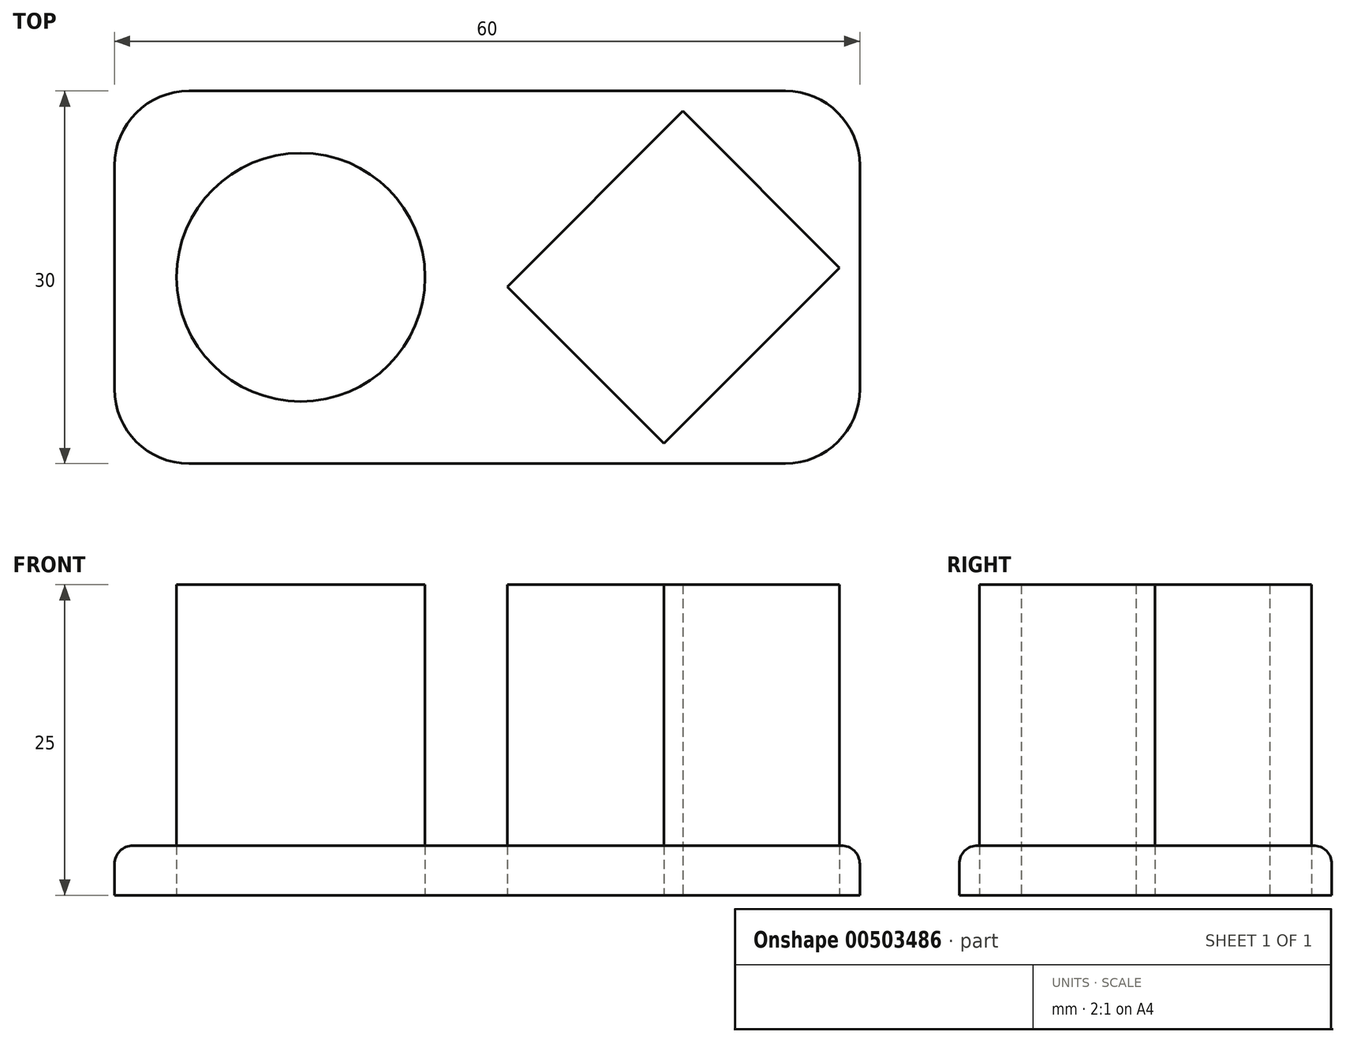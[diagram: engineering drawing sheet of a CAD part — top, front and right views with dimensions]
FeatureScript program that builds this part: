
annotation { "Feature Type Name" : "Feature", "Feature Type Description" : "" }
export const myFeature = defineFeature(function(context is Context, id is Id, definition is map)
    precondition{}
    {
        {
            var Q0;
            Q0=qCreatedBy(makeId("Top.planeOp"),FACE);
            var sketch = newSketch(context, id + "F0", { "sketchPlane" : qUnion([Q0])});
            skLineSegment(sketch, "E0.bottom", {"start": v(30, -15) * mm, "end": v(-30, -15) * mm});
            skLineSegment(sketch, "E0.top", {"start": v(30, 15) * mm, "end": v(-30, 15) * mm});
            skLineSegment(sketch, "E0.left", {"start": v(30, -15) * mm, "end": v(30, 15) * mm});
            skLineSegment(sketch, "E0.right", {"start": v(-30, -15) * mm, "end": v(-30, 15) * mm});
            skPoint(sketch, "E0.middle", {"position": v(0, 0) * mm});
            skSolve(sketch);
        }
        {
            var Q0;
            Q0 = qSketchRegion(id + "F0", true);
            extrude(context, id + "F1", {"entities" : qUnion([Q0]), "depth" : 4 * mm});
        }
        {
            var Q0;
            Q0=qCreatedBy(makeId("Top.planeOp"),FACE);
            var sketch = newSketch(context, id + "F2", { "sketchPlane" : qUnion([Q0])});
            skLineSegment(sketch, "E1", {"start": v(0, 0) * mm, "end": v(15, 0) * mm});
            skLineSegment(sketch, "E2", {"start": v(0, 0) * mm, "end": v(-15, 0) * mm});
            skCircle(sketch, "E3", {"center": v(-15, 0) * mm, "radius": 10 * mm});
            skLineSegment(sketch, "E4.bottom", {"start": v(25, -8.92) * mm, "end": v(5, -8.92) * mm});
            skLineSegment(sketch, "E4.top", {"start": v(25, 8.92) * mm, "end": v(5, 8.92) * mm});
            skLineSegment(sketch, "E4.left", {"start": v(25, -8.92) * mm, "end": v(25, 8.92) * mm});
            skLineSegment(sketch, "E4.right", {"start": v(5, -8.92) * mm, "end": v(5, 8.92) * mm});
            skPoint(sketch, "E4.middle", {"position": v(15, 0) * mm});
            skSolve(sketch);
        }
        {
            var Q0;
            Q0 = qSketchRegion(id + "F2", true);
            extrude(context, id + "F3", {"entities" : qUnion([Q0]), "depth" : 25 * mm});
        }
        {
            var Q0;
            Q0=qCreatedBy(makeId("Front.planeOp"),FACE);
            var sketch = newSketch(context, id + "F4", { "sketchPlane" : qUnion([Q0])});
            skLineSegment(sketch, "E5", {"start": v(0, 0) * mm, "end": v(15, 0) * mm});
            skLineSegment(sketch, "E6", {"start": v(15, 0) * mm, "end": v(15, 40) * mm});
            skSolve(sketch);
        }
        {
            var Q0;
            Q0=makeQuery(id+"F3.opExtrude","SWEPT_BODY",BODY,{"disambiguationData":[OSD([sQuery(id+"F2.wireOp",EDGE,"E4.bottom"),sQuery(id+"F2.wireOp",EDGE,"E4.top"),sQuery(id+"F2.wireOp",EDGE,"E4.left"),sQuery(id+"F2.wireOp",EDGE,"E4.right")])]});
            var Q1;
            Q1=sQuery(id+"F4.wireOp",EDGE,"E6");
            transform(context, id + "F5", {"entities" : qUnion([Q0]), "transformType" : TransformType.ROTATION, "transformAxis" : qUnion([Q1]), "angle" : 45 * degree, "makeCopy" : false});
        }
        {
            var Q0;
            Q0=makeQuery(id+"F1.opExtrude","SWEPT_EDGE",EDGE,{"disambiguationData":[OSD([sQuery(id+"F0.wireOp",EDGE,"E0.bottom"),sQuery(id+"F0.wireOp",EDGE,"E0.right")])]});
            var Q1;
            Q1=makeQuery(id+"F1.opExtrude","SWEPT_EDGE",EDGE,{"disambiguationData":[OSD([sQuery(id+"F0.wireOp",EDGE,"E0.bottom"),sQuery(id+"F0.wireOp",EDGE,"E0.left")])]});
            var Q2;
            Q2=makeQuery(id+"F1.opExtrude","SWEPT_EDGE",EDGE,{"disambiguationData":[OSD([sQuery(id+"F0.wireOp",EDGE,"E0.top"),sQuery(id+"F0.wireOp",EDGE,"E0.left")])]});
            var Q3;
            Q3=makeQuery(id+"F1.opExtrude","SWEPT_EDGE",EDGE,{"disambiguationData":[OSD([sQuery(id+"F0.wireOp",EDGE,"E0.top"),sQuery(id+"F0.wireOp",EDGE,"E0.right")])]});
            fillet(context, id + "F6", {"entities" : qUnion([Q0, Q1, Q2, Q3]), "radius" : 6 * mm, "tangentPropagation" : true, "allowEdgeOverflow" : false});
        }
        {
            var Q0;
            Q0=makeQuery(id+"F1.opExtrude","CAP_EDGE",EDGE,{"disambiguationData":[OSD([sQuery(id+"F0.wireOp",EDGE,"E0.bottom")])],"isStart":false});
            fillet(context, id + "F7", {"entities" : qUnion([Q0]), "radius" : 1.5 * mm, "tangentPropagation" : true, "allowEdgeOverflow" : false});
        }
    });
